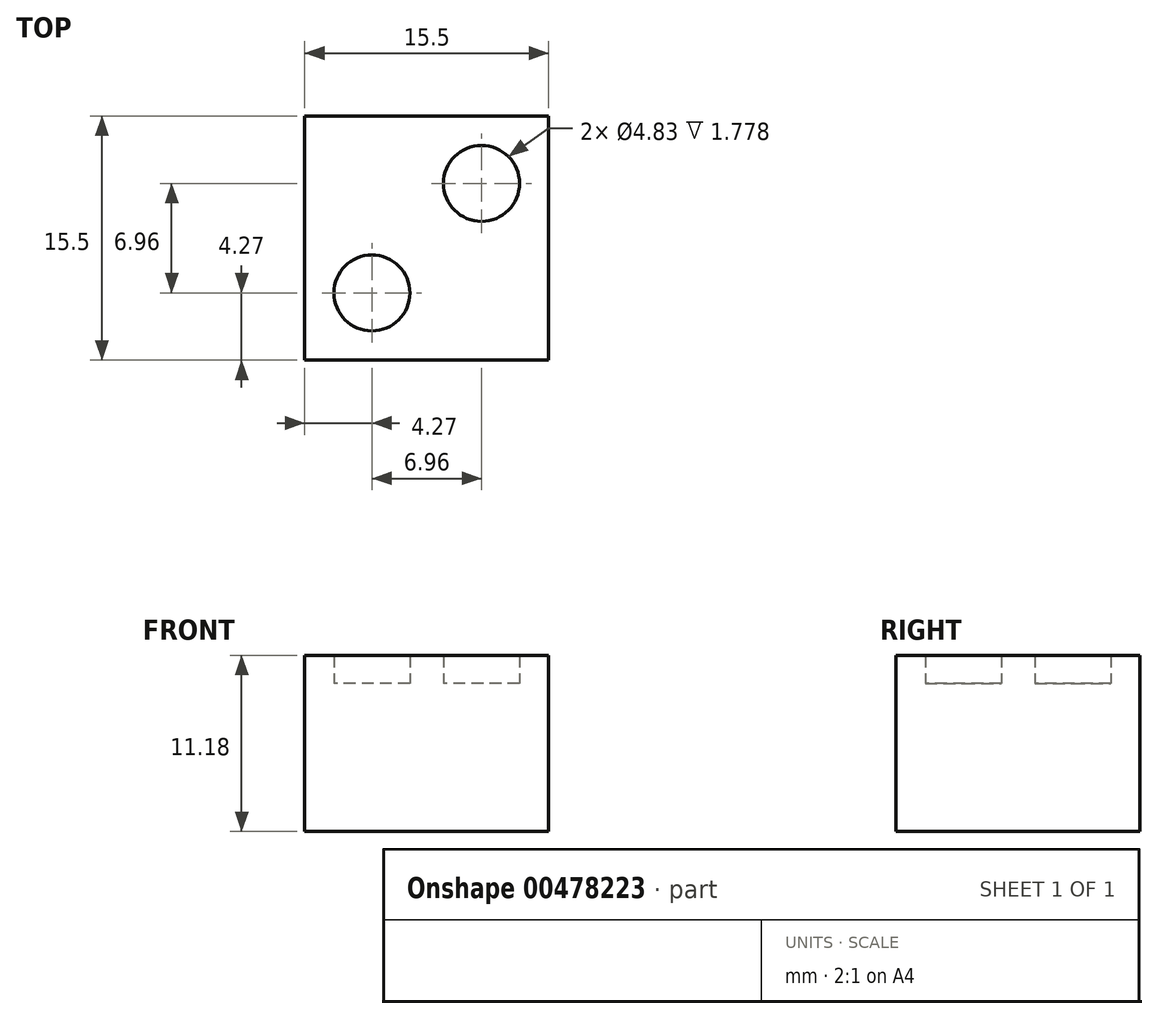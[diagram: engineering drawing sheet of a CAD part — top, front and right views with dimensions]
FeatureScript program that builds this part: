
annotation { "Feature Type Name" : "Feature", "Feature Type Description" : "" }
export const myFeature = defineFeature(function(context is Context, id is Id, definition is map)
    precondition{}
    {
        {
            var Q0;
            Q0=qCreatedBy(makeId("Top.planeOp"),FACE);
            var sketch = newSketch(context, id + "F0", { "sketchPlane" : qUnion([Q0])});
            skLineSegment(sketch, "E0.bottom", {"start": v(-7.75, 7.75) * mm, "end": v(7.75, 7.75) * mm});
            skLineSegment(sketch, "E0.top", {"start": v(-7.75, -7.75) * mm, "end": v(7.75, -7.75) * mm});
            skLineSegment(sketch, "E0.left", {"start": v(-7.75, 7.75) * mm, "end": v(-7.75, -7.75) * mm});
            skLineSegment(sketch, "E0.right", {"start": v(7.75, 7.75) * mm, "end": v(7.75, -7.75) * mm});
            skPoint(sketch, "E0.middle", {"position": v(0, 0) * mm});
            skSolve(sketch);
        }
        {
            var Q0;
            Q0=makeQuery(id+"F0.imprint","IMPRINT",FACE,{"disambiguationData":[TD([[makeQuery(id+"F0.imprint","IMPRINT",EDGE,{"derivedFrom":sQuery(id+"F0.wireOp",EDGE,"E0.bottom")}),-1.0]])]});
            extrude(context, id + "F1", {"entities" : qUnion([Q0]), "depth" : 9.4 * mm, "offsetDistance" : 25.4 * mm});
        }
        {
            var Q0;
            Q0=makeQuery(id+"F1.opExtrude","CAP_FACE",FACE,{"disambiguationData":[OSD([sQuery(id+"F0.wireOp",EDGE,"E0.bottom"),sQuery(id+"F0.wireOp",EDGE,"E0.top"),sQuery(id+"F0.wireOp",EDGE,"E0.left"),sQuery(id+"F0.wireOp",EDGE,"E0.right")])],"isStart":false});
            var sketch = newSketch(context, id + "F2", { "sketchPlane" : qUnion([Q0])});
            skCircle(sketch, "E1", {"center": v(-3.48, 3.48) * mm, "radius": 2.41 * mm});
            skCircle(sketch, "E2.MirrorC", {"center": v(3.48, 3.48) * mm, "radius": 2.41 * mm});
            skCircle(sketch, "E3.MirrorC", {"center": v(-3.48, -3.48) * mm, "radius": 2.41 * mm});
            skCircle(sketch, "E4.MirrorC", {"center": v(3.48, -3.48) * mm, "radius": 2.41 * mm});
            skSolve(sketch);
        }
        {
            var Q0;
            Q0=makeQuery(id+"F2.imprint","IMPRINT",FACE,{"disambiguationData":[TD([[makeQuery(id+"F2.imprint","IMPRINT",EDGE,{"derivedFrom":sQuery(id+"F2.wireOp",EDGE,"E1")}),1.0]])]});
            var Q1;
            Q1=makeQuery(id+"F2.imprint","IMPRINT",FACE,{"disambiguationData":[TD([[makeQuery(id+"F2.imprint","IMPRINT",EDGE,{"derivedFrom":sQuery(id+"F2.wireOp",EDGE,"E2.MirrorC")}),-1.0]])]});
            var Q2;
            Q2=makeQuery(id+"F2.imprint","IMPRINT",FACE,{"disambiguationData":[TD([[makeQuery(id+"F2.imprint","IMPRINT",EDGE,{"derivedFrom":sQuery(id+"F2.wireOp",EDGE,"E4.MirrorC")}),1.0]])]});
            var Q3;
            Q3=makeQuery(id+"F2.imprint","IMPRINT",FACE,{"disambiguationData":[TD([[makeQuery(id+"F2.imprint","IMPRINT",EDGE,{"derivedFrom":sQuery(id+"F2.wireOp",EDGE,"E3.MirrorC")}),-1.0]])]});
            extrude(context, id + "F3", {"entities" : qUnion([Q0, Q1, Q2, Q3]), "operationType" : NewBodyOperationType.ADD, "depth" : 1.78 * mm, "offsetDistance" : 25.4 * mm});
        }
    });
